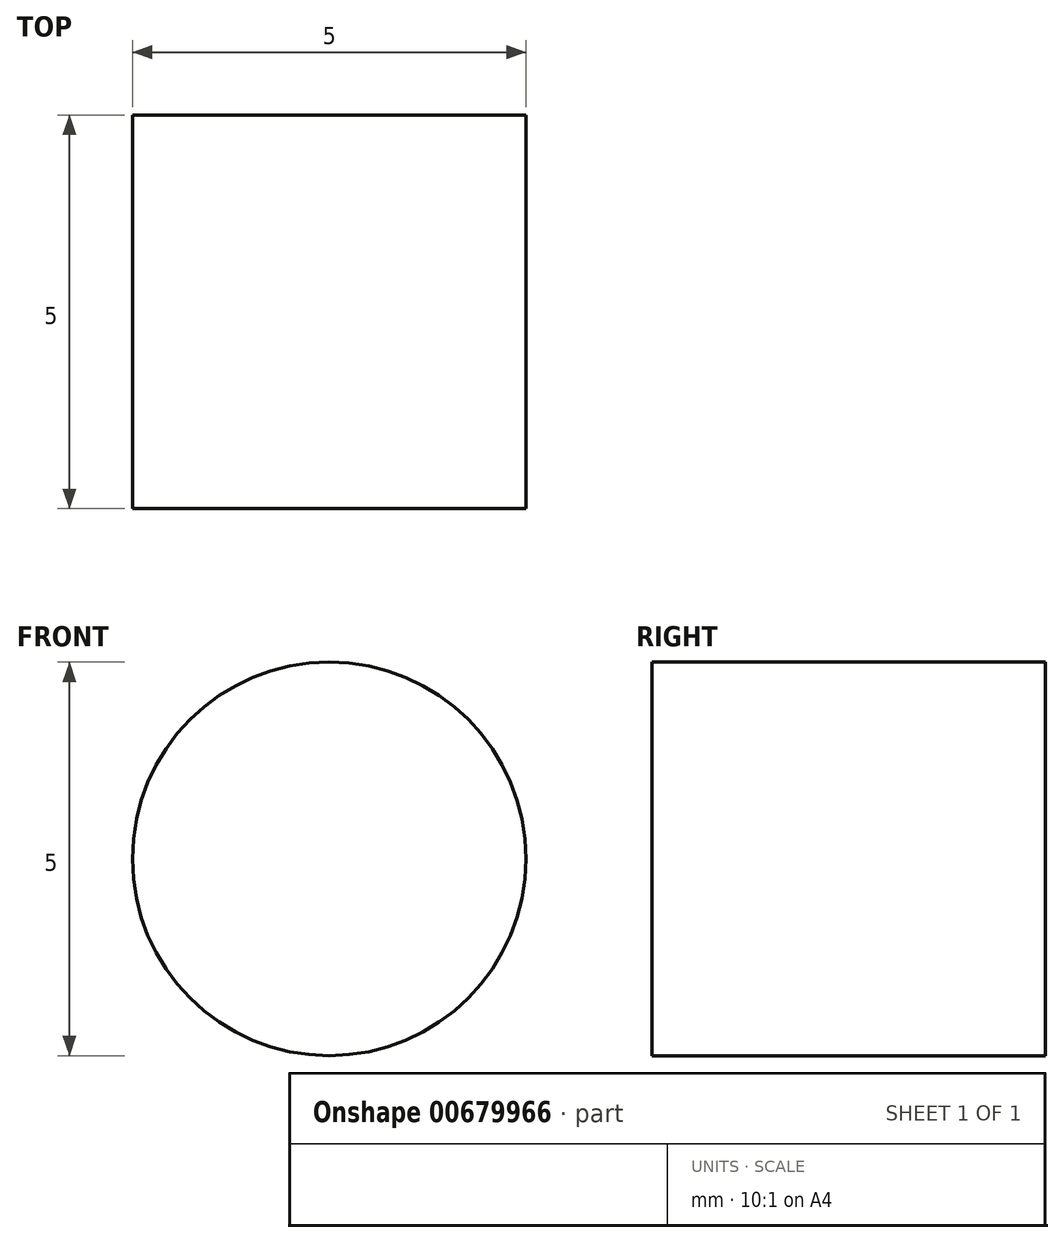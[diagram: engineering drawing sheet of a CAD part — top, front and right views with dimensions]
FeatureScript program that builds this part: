
annotation { "Feature Type Name" : "Feature", "Feature Type Description" : "" }
export const myFeature = defineFeature(function(context is Context, id is Id, definition is map)
    precondition{}
    {
        {
            var Q0;
            Q0=qCreatedBy(makeId("Front.planeOp"),FACE);
            var sketch = newSketch(context, id + "F0", { "sketchPlane" : qUnion([Q0])});
            skCircle(sketch, "E0", {"center": v(0, -0.18) * mm, "radius": 2.5 * mm});
            skSolve(sketch);
        }
        {
            var Q0;
            Q0 = qSketchRegion(id + "F0", true);
            extrude(context, id + "F1", {"entities" : qUnion([Q0]), "depth" : 5 * mm, "offsetDistance" : 25.4 * mm});
        }
    });
